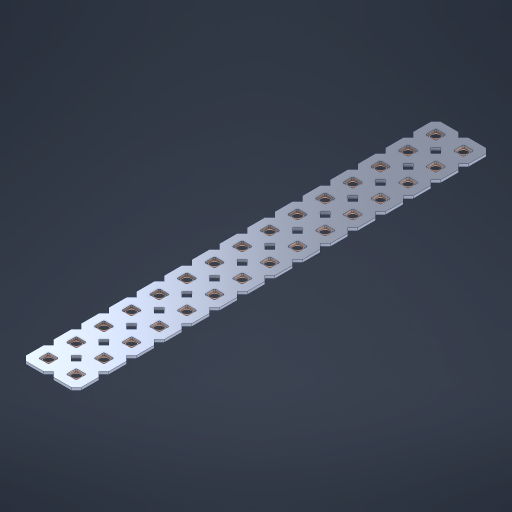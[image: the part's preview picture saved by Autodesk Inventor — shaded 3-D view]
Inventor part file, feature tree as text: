
AUTODESK INVENTOR PART (.ipt)
format: ipt  version: 2023 (Build 270158000, 158)  size: 599,552 bytes
history: native  units: in
note: dims shown in document units (in); Inventor stores cm internally (conversion verified against a paired STEP export)
features: other x31, extrude x29, sketch x2, pattern_linear x1
ambient origin geometry x8: Origin, YZ Plane, XZ Plane, XY Plane, X Axis, Y Axis, Z Axis, Center Point
bodies: Solid1 (feature_tree), Body (feature_tree)
feature tree (63):
  pattern_linear  "Rectangular Pattern1"  Spacing1=0.09in  [1 undecoded]
  sketch  "Sketch1"  dims[d1=0.5in]
  sketch  "Sketch2"  dims[d2=0.182in d3=0.09in d4=0.09in d5=0.09in d6=0.09in d7=0.09in d8=0.09in d9=0.09in d10=0.09in d11=0.02in d13=0.0in d14=0.172in d15=0.0625in d16=0.0in d19=0.5in d22=0.5in]
  other  "Srf1"
  other  "Srf126"
  other  "Srf127"
  other  "Srf128"
  other  "Srf129"
  other  "Srf130"
  other  "Srf131"
  other  "Srf250"
  other  "Srf251"
  other  "Srf252"
  other  "Srf253"
  other  "Srf254"
  other  "Srf255"
  other  "Srf256"
  other  "Srf257"
  other  "Srf268"
  other  "Srf269"
  other  "Srf270"
  other  "Srf271"
  other  "Srf272"
  other  "Srf273"
  other  "Srf274"
  other  "Srf275"
  other  "Srf276"
  other  "Srf277"
  other  "Srf278"
  other  "Srf279"
  other  "Srf280"
  other  "Srf281"
  other  "Srf282"
  other  "Circle"
  extrude  "ExtrusionSrf126"  Depth=0.09in
  extrude  "ExtrusionSrf127"  Depth=0.09in
  extrude  "ExtrusionSrf128"  Depth=0.09in
  extrude  "ExtrusionSrf129"  Depth=0.09in
  extrude  "ExtrusionSrf130"  Depth=0.09in
  extrude  "ExtrusionSrf131"  Depth=0.09in
  extrude  "ExtrusionSrf250"  Depth=0.09in
  extrude  "ExtrusionSrf251"  Depth=0.02in
  extrude  "ExtrusionSrf252"  TaperAngle=0.0deg  [1 undecoded]
  extrude  "ExtrusionSrf253"  Depth=0.5in
  extrude  "ExtrusionSrf254"  Depth=0.5in TaperAngle=0.0deg
  extrude  "ExtrusionSrf255"  Depth=0.5in
  extrude  "ExtrusionSrf256"  Depth=0.5in
  extrude  "ExtrusionSrf257"  [1 undecoded]
  extrude  "ExtrusionSrf268"  [1 undecoded]
  extrude  "ExtrusionSrf269"  [1 undecoded]
  extrude  "ExtrusionSrf270"  [1 undecoded]
  extrude  "ExtrusionSrf271"  [1 undecoded]
  extrude  "ExtrusionSrf272"  [1 undecoded]
  extrude  "ExtrusionSrf273"  [1 undecoded]
  extrude  "ExtrusionSrf274"  [1 undecoded]
  extrude  "ExtrusionSrf275"  [1 undecoded]
  extrude  "ExtrusionSrf276"  [1 undecoded]
  extrude  "ExtrusionSrf277"  [1 undecoded]
  extrude  "ExtrusionSrf278"  [1 undecoded]
  extrude  "ExtrusionSrf279"  [1 undecoded]
  extrude  "ExtrusionSrf280"  [1 undecoded]
  extrude  "ExtrusionSrf281"  [1 undecoded]
  extrude  "ExtrusionSrf282"  [1 undecoded]
note: 18 required parameter values undecoded (feature->parameter linkage not recoverable at this tier; creation-order binding heuristic only, values carry confidence <= 0.55)
